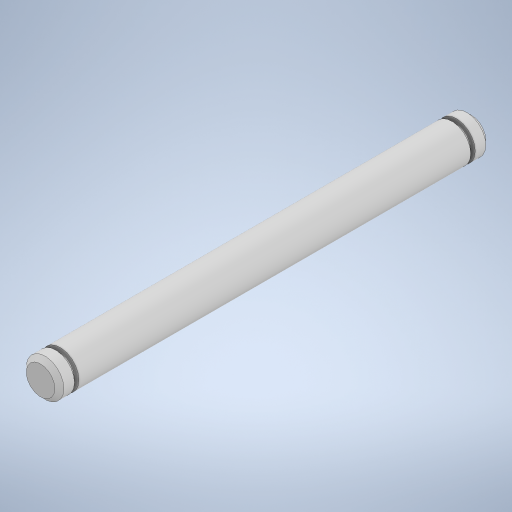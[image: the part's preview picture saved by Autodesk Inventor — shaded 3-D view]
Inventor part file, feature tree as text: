
AUTODESK INVENTOR PART (.ipt)
format: ipt  version: 2024 (Build 280153000, 153)  size: 261,120 bytes
history: native  units: in
note: dims shown in document units (in); Inventor stores cm internally (conversion verified against a paired STEP export)
features: extrude x3, sketch x3, chamfer x1, mirror x1, direct_edit x1, other x1
ambient origin geometry x8: Origin, YZ Plane, XZ Plane, XY Plane, X Axis, Y Axis, Z Axis, Center Point
bodies: Solid1 (feature_tree)
feature tree (10):
  extrude  "Extrusion1"  Depth=1.2998in TaperAngle=0.0deg
  extrude  "Extrusion2"  Depth=0.015in TaperAngle=0.0deg
  extrude  "Extrusion3"  Depth=0.3937in TaperAngle=0.0deg
  chamfer  "Chamfer1"  Distance=0.015in Angle=45.0deg
  mirror  "Mirror1"
  direct_edit  "Direct Edit1"
  sketch  "Sketch1"  dims[d0=0.125in d1=1.2998in d2=0.0in]
  sketch  "Sketch2"  dims[d3=0.0938in d4=0.015in d5=0.0in]
  sketch  "Sketch3"  dims[d6=0.125in d7=0.05in d8=0.0in d9=0.015in d10=0.125in d11=45.0deg d12=3.937in d13=0.3937in d14=0.3937in]
  other  "Scale1"
